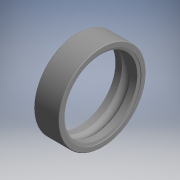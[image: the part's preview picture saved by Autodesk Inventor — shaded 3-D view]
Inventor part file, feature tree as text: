
AUTODESK INVENTOR PART (.ipt)
format: ipt  version: 2017.3 (Build 213256000, 256)  size: 154,112 bytes
history: native  units: mm (DEFAULTED — no unit token found)
features: revolve x1, sketch x1
ambient origin geometry x8: Origin, YZ Plane, XZ Plane, XY Plane, X Axis, Y Axis, Z Axis, Center Point
bodies: Solid1 (feature_tree)
feature tree (2):
  revolve  "Revolution1"  [1 undecoded]
  sketch  "Sketch_17"  dims[d0=360.0deg]
note: 1 required parameter value undecoded (feature->parameter linkage not recoverable at this tier; creation-order binding heuristic only, values carry confidence <= 0.55)
